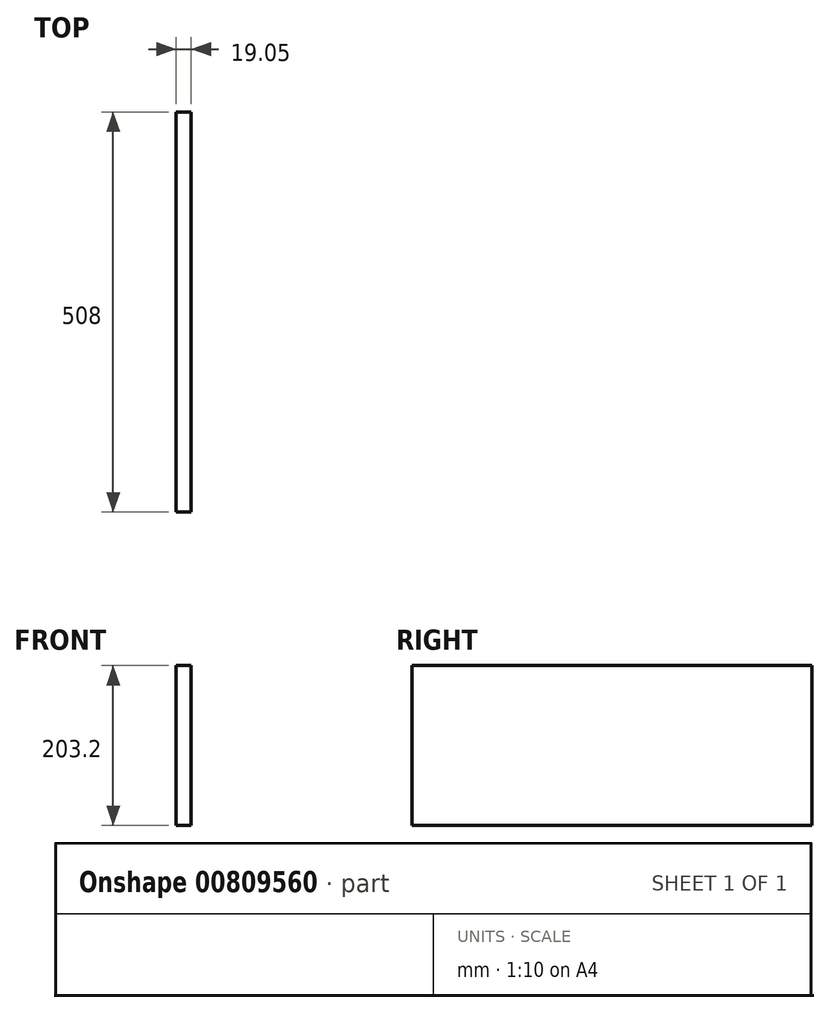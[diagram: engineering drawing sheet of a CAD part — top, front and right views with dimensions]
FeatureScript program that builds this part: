
annotation { "Feature Type Name" : "Feature", "Feature Type Description" : "" }
export const myFeature = defineFeature(function(context is Context, id is Id, definition is map)
    precondition{}
    {
        {
            var Q0;
            Q0=qCreatedBy(makeId("Right.planeOp"),FACE);
            var sketch = newSketch(context, id + "F0", { "sketchPlane" : qUnion([Q0])});
            skLineSegment(sketch, "E0.bottom", {"start": v(254, -101.6) * mm, "end": v(-254, -101.6) * mm});
            skLineSegment(sketch, "E0.top", {"start": v(254, 101.6) * mm, "end": v(-254, 101.6) * mm});
            skLineSegment(sketch, "E0.left", {"start": v(254, -101.6) * mm, "end": v(254, 101.6) * mm});
            skLineSegment(sketch, "E0.right", {"start": v(-254, -101.6) * mm, "end": v(-254, 101.6) * mm});
            skPoint(sketch, "E0.middle", {"position": v(0, 0) * mm});
            skSolve(sketch);
        }
        {
            var Q0;
            Q0=makeQuery(id+"F0.imprint","IMPRINT",FACE,{"disambiguationData":[TD([[makeQuery(id+"F0.imprint","IMPRINT",EDGE,{"derivedFrom":sQuery(id+"F0.wireOp",EDGE,"E0.bottom")}),-1.0]])]});
            extrude(context, id + "F1", {"entities" : qUnion([Q0]), "depth" : 19.05 * mm, "offsetDistance" : 25.4 * mm});
        }
    });
